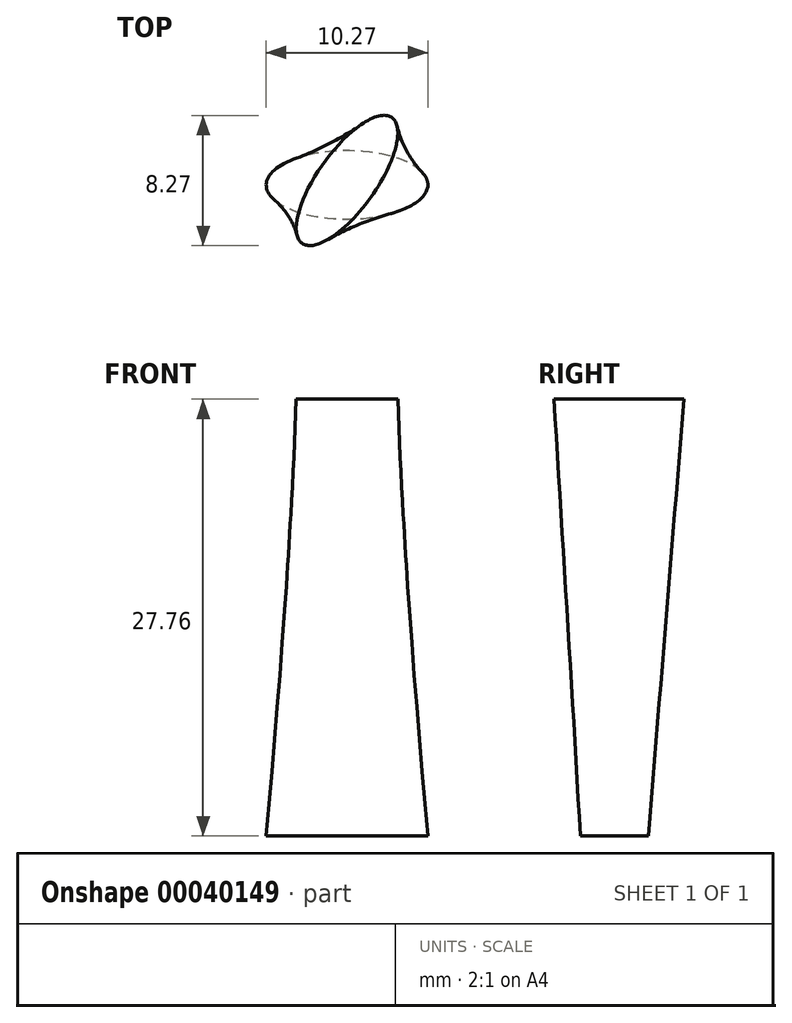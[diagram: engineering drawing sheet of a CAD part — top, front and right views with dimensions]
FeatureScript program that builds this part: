
annotation { "Feature Type Name" : "Feature", "Feature Type Description" : "" }
export const myFeature = defineFeature(function(context is Context, id is Id, definition is map)
    precondition{}
    {
        {
            var Q0;
            Q0=qCreatedBy(makeId("Top.planeOp"),FACE);
            cPlane(context, id + "F0", {"entities" : qUnion([Q0]), "cplaneType" : CPlaneType.OFFSET, "offset" : 27.76 * mm, "width" : 152.4 * mm, "height" : 152.4 * mm});
        }
        {
            var Q0;
            Q0=qCreatedBy(makeId("Top.planeOp"),FACE);
            var sketch = newSketch(context, id + "F1", { "sketchPlane" : qUnion([Q0])});
            skEllipse(sketch, "E0", {"center": v(-53.63, -28.1) * mm, "majorRadius": 5.13 * mm, "minorRadius": 2.17 * mm, "majorAxis": v(1, 0)});
            skSolve(sketch);
        }
        {
            var Q0;
            Q0=qCreatedBy(id+"F0.planeOp",FACE);
            var sketch = newSketch(context, id + "F2", { "sketchPlane" : qUnion([Q0])});
            skEllipse(sketch, "E1", {"center": v(-53.63, -27.81) * mm, "majorRadius": 4.9 * mm, "minorRadius": 1.85 * mm, "majorAxis": v(0.58, 0.81)});
            skSolve(sketch);
        }
        {
            var Q0;
            Q0 = qSketchRegion(id + "F1", true);
            var Q1;
            Q1 = qSketchRegion(id + "F2", true);
            loft(context, id + "F3", {"sheetProfilesArray" : [{ "sheetProfileEntities" : qUnion([Q0]) }, { "sheetProfileEntities" : qUnion([Q1]) }]});
        }
    });
